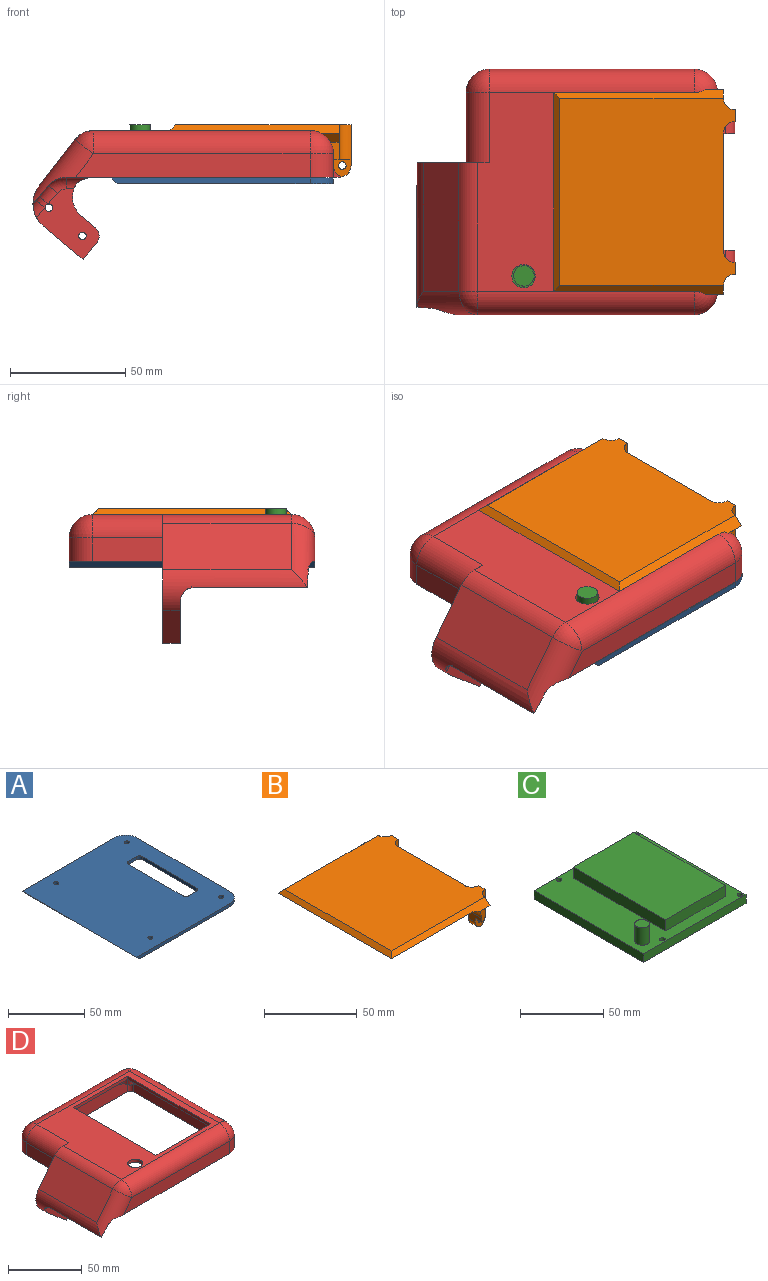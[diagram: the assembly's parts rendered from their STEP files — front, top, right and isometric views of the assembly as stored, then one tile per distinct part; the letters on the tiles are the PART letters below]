
ASSEMBLY  parts=4 mates=3
PART A: 20 faces, bbox 96.5x106.7x2.5 mm
  f0: plane 106.68x96.52mm, normal (0,0,1), area 9514.1mm2, adj f2,f3,f4,f5,f6,f7,f8,f9
  f1: plane 106.68x93.98mm, normal (0,0,-1), area 9243.1mm2, adj f2,f3,f4,f5,f6,f7,f8,f9
  f2: plane 86.36x2.54mm, normal (0,-1,0), area 216.1mm2, adj f0,f1,f17,f19
  f3: plane 86.36x2.54mm, normal (1,0,0), area 219.4mm2, adj f0,f1,f17,f18
  f4: plane 86.36x2.54mm, normal (0,1,0), area 216.1mm2, adj f0,f1,f18,f19
  f5: cylinder r=1.65mm len=3.3mm, axis (0,0,-1), area 26.3mm2, adj f0,f1
  f6: cylinder r=1.65mm len=3.3mm, axis (0,0,-1), area 26.3mm2, adj f0,f1
  f7: cylinder r=1.65mm len=3.3mm, axis (0,0,-1), area 26.3mm2, adj f0,f1
  f8: cylinder r=1.65mm len=3.3mm, axis (0,0,-1), area 26.3mm2, adj f0,f1
  f9: plane 50.8x2.54mm, normal (1,0,0), area 129mm2, adj f0,f1,f13,f16
  f10: plane 7.62x2.54mm, normal (0,-1,0), area 19.4mm2, adj f0,f1,f15,f16
  f11: plane 50.8x2.54mm, normal (-1,0,0), area 129mm2, adj f0,f1,f14,f15
  f12: plane 7.62x2.54mm, normal (0,1,0), area 19.4mm2, adj f0,f1,f13,f14
  f13: cylinder r=2.54mm len=2.54mm, axis (0,0,1), area 10.1mm2, adj f0,f1,f9,f12
  f14: cylinder r=2.54mm len=2.54mm, axis (0,0,-1), area 10.1mm2, adj f0,f1,f11,f12
  f15: cylinder r=2.54mm len=2.54mm, axis (0,0,1), area 10.1mm2, adj f0,f1,f10,f11
  f16: cylinder r=2.54mm len=2.54mm, axis (0,0,-1), area 10.1mm2, adj f0,f1,f9,f10
  f17: cylinder r=10.16mm len=10.16mm, axis (0,0,-1), area 40.5mm2, adj f0,f1,f2,f3
  f18: cylinder r=10.16mm len=10.16mm, axis (0,0,1), area 40.5mm2, adj f0,f1,f3,f4
  f19: plane 106.68x2.54mm, normal (-0.71,0,-0.71), area 383.2mm2, adj f0,f1,f2,f4
PART B: 43 faces, bbox 78.7x88.9x22.7 mm
  f0: plane 7.62x3.9mm, normal (0,-1,0), area 21.6mm2, adj f7,f24,f25,f27,f42
  f1: plane 7.62x3.9mm, normal (0,1,0), area 21.6mm2, adj f3,f8,f25,f26,f41
  f2: plane 49.69x2.54mm, normal (-1,0,0), area 119.7mm2, adj f4,f25,f34,f35
  f3: plane 10.03x5.08mm, normal (-1,0,0), area 38.4mm2, adj f1,f8,f10,f11,f21,f25
  f4: plane 40.89x2.54mm, normal (0,0,-1), area 103.9mm2, adj f2,f9,f34,f35
  f5: cylinder r=5.08mm len=12.7mm, axis (0,0,-1), area 100.7mm2, adj f9,f15,f16,f31,f32
  f6: cylinder r=5.08mm len=12.7mm, axis (0,0,1), area 100.7mm2, adj f9,f15,f17,f29,f33
  f7: plane 10.03x5.08mm, normal (-1,0,0), area 38.4mm2, adj f0,f12,f13,f23,f24,f25
  f8: plane 7.62x4.95mm, normal (0,0,-1), area 18.1mm2, adj f1,f3,f10,f26
  f9: plane 51.05x15.24mm, normal (1,0,0), area 767.8mm2, adj f4,f5,f6,f15,f32,f33,f34,f35
  f10: plane 22.7x7.62mm, normal (0,1,0), area 38.6mm2, adj f3,f8,f15,f16,f19,f20,f21,f26
  f11: plane 13.39x8.2mm, normal (0,-1,0), area 61mm2, adj f3,f16,f19,f20,f21,f25,f31,f32
  f12: plane 13.39x8.2mm, normal (0,1,0), area 61mm2, adj f7,f17,f18,f22,f23,f25,f29,f33
  f13: plane 22.7x7.62mm, normal (0,-1,0), area 38.6mm2, adj f7,f15,f17,f18,f22,f23,f24,f27
  f14: plane 86.36x60.96mm, normal (0,0,-1), area 5264.5mm2, adj f25,f38,f39,f40
  f15: plane 81.28x76.2mm, normal (0,0,1), area 5854.4mm2, adj f5,f6,f9,f10,f13,f16,f17,f26
  f16: plane 17.78x5.08mm, normal (1,0,0), area 90.3mm2, adj f5,f10,f11,f15,f20
  f17: plane 17.78x5.08mm, normal (1,0,0), area 90.3mm2, adj f6,f12,f13,f15,f22
  f18: cylinder r=1.65mm len=5.08mm, axis (0,-1,0), area 52.7mm2, adj f12,f13
  f19: cylinder r=1.65mm len=5.08mm, axis (0,-1,0), area 52.7mm2, adj f10,f11
  f20: cylinder r=5.08mm len=5.08mm, axis (0,-1,0), area 34mm2, adj f10,f11,f16,f21
  f21: cylinder r=5.08mm len=5.08mm, axis (0,-1,0), area 34mm2, adj f3,f10,f11,f20
  f22: cylinder r=5.08mm len=5.08mm, axis (0,-1,0), area 34mm2, adj f12,f13,f17,f23
  f23: cylinder r=5.08mm len=5.08mm, axis (0,-1,0), area 34mm2, adj f7,f12,f13,f22
  f24: plane 7.62x4.95mm, normal (0,0,-1), area 18.1mm2, adj f0,f7,f13,f27
  f25: cylinder r=10.16mm len=88.9mm, axis (0,1,0), area 1314.3mm2, adj f0,f1,f2,f3,f7,f11,f12,f14
  f26: cylinder r=5.08mm len=15.24mm, axis (0,0,1), area 119.7mm2, adj f1,f8,f10,f15,f36
  f27: cylinder r=5.08mm len=15.24mm, axis (0,0,1), area 119.7mm2, adj f0,f13,f15,f24,f37
  f28: plane 0.85x0.39mm, normal (0,-1,0), area 0mm2, adj f25,f33,f35
  f29: plane 3.41x1.32mm, normal (0,0,-1), area 1.4mm2, adj f6,f12,f33
  f30: plane 0.85x0.39mm, normal (0,1,0), area 0mm2, adj f25,f32,f34
  f31: plane 3.41x1.32mm, normal (0,0,-1), area 1.4mm2, adj f5,f11,f32
  f32: cylinder r=5.08mm len=5.61mm, axis (0,1,0), area 28.1mm2, adj f5,f9,f11,f25,f30,f31,f34
  f33: cylinder r=5.08mm len=5.61mm, axis (0,1,0), area 28.1mm2, adj f6,f9,f12,f25,f28,f29,f35
  f34: cylinder r=5.08mm len=5.08mm, axis (-1,0,0), area 16.6mm2, adj f2,f4,f9,f25,f30,f32
  f35: cylinder r=5.08mm len=5.08mm, axis (1,0,0), area 16.6mm2, adj f2,f4,f9,f25,f28,f33
  f36: plane 7.62x3.81mm, normal (1,0,0), area 14.5mm2, adj f26,f40,f41
  f37: plane 7.62x3.81mm, normal (1,0,0), area 14.5mm2, adj f27,f38,f42
  f38: plane 73.66x3.81mm, normal (0,-0.71,0.71), area 276.9mm2, adj f14,f15,f25,f37,f39,f42
  f39: plane 86.36x2.54mm, normal (-0.71,0,0.71), area 301.1mm2, adj f14,f15,f38,f40
  f40: plane 73.66x3.81mm, normal (0,0.71,0.71), area 276.9mm2, adj f14,f15,f25,f36,f39,f41
  f41: plane 7.78x3.81mm, normal (0,0.71,-0.71), area 29.6mm2, adj f1,f25,f36,f40
  f42: plane 7.78x3.81mm, normal (0,-0.71,-0.71), area 29.6mm2, adj f0,f25,f37,f38
PART C: 17 faces, bbox 87.1x93.2x19.1 mm
  f0: plane 87.12x6.35mm, normal (0,1,0), area 553.2mm2, adj f1,f7,f8,f9
  f1: plane 93.22x6.35mm, normal (-1,0,0), area 591.9mm2, adj f0,f2,f8,f9
  f2: plane 87.12x6.35mm, normal (0,-1,0), area 553.2mm2, adj f1,f7,f8,f9
  f3: cylinder r=1.65mm len=6.35mm, axis (0,0,-1), area 65.9mm2, adj f8,f9
  f4: cylinder r=1.65mm len=6.35mm, axis (0,0,-1), area 65.9mm2, adj f8,f9
  f5: cylinder r=1.65mm len=6.35mm, axis (0,0,-1), area 65.9mm2, adj f8,f9
  f6: cylinder r=1.65mm len=6.35mm, axis (0,0,-1), area 65.9mm2, adj f8,f9
  f7: plane 93.22x6.35mm, normal (1,0,0), area 591.9mm2, adj f0,f2,f8,f9
  f8: plane 93.22x87.12mm, normal (0,0,1), area 4047mm2, adj f0,f1,f2,f3,f4,f5,f6,f7
  f9: plane 93.22x87.12mm, normal (0,0,-1), area 8087.1mm2, adj f0,f1,f2,f3,f4,f5,f6,f7
  f10: plane 78x8.13mm, normal (1,0,0), area 634mm2, adj f8,f11,f13,f14
  f11: plane 51x8.13mm, normal (0,1,0), area 414.5mm2, adj f8,f10,f12,f14
  f12: plane 78x8.13mm, normal (-1,0,0), area 634mm2, adj f8,f11,f13,f14
  f13: plane 51x8.13mm, normal (0,-1,0), area 414.5mm2, adj f8,f10,f12,f14
  f14: plane 78x51mm, normal (0,0,1), area 3978mm2, adj f10,f11,f12,f13
  f15: cylinder r=4.45mm len=12.7mm, axis (0,0,-1), area 354.7mm2, adj f8,f16
  f16: plane 8.89x8.89mm, normal (0,0,1), area 62.1mm2, adj f15
PART D: 86 faces, bbox 140.6x106.8x56.1 mm
  f0: plane 12.7x10.16mm, normal (1,0,0), area 129mm2, adj f34,f55,f70,f78
  f1: plane 12.7x10.16mm, normal (1,0,0), area 129mm2, adj f34,f54,f70,f75
  f2: plane 94.08x86.36mm, normal (0,0,1), area 3736.2mm2, adj f8,f21,f22,f23,f24,f25,f53,f66
  f3: plane 17.38x7.02mm, normal (0,0,-1), area 48.2mm2, adj f12,f26,f37,f58,f59
  f4: plane 11.98x11.92mm, normal (0,0,-1), area 46.3mm2, adj f13,f28,f37,f38,f56,f60,f61
  f5: plane 11.98x11.92mm, normal (0,0,-1), area 46.3mm2, adj f14,f30,f35,f38,f57,f62,f63
  f6: plane 17.38x7.02mm, normal (0,0,-1), area 48.2mm2, adj f15,f32,f35,f64,f65
  f7: plane 17.2x14.43mm, normal (-0.64,0,-0.77), area 171.1mm2, adj f8,f41,f42,f85
  f8: plane 55.96x31.46mm, normal (0,1,0), area 736.3mm2, adj f2,f7,f10,f19,f20,f34,f39,f40
  f9: plane 50.65x8.07mm, normal (0.77,0,-0.64), area 520.1mm2, adj f43,f48,f50,f51,f74,f85
  f10: plane 30.48x10.16mm, normal (-1,0,0), area 309.7mm2, adj f8,f34,f52,f66
  f11: plane 94.23x89.41mm, normal (0,0,-1), area 3968.5mm2, adj f12,f13,f14,f15,f21,f22,f23,f24
  f12: cylinder r=3.81mm len=7.62mm, axis (0,0,1), area 78.9mm2, adj f3,f11,f58,f59
  f13: cylinder r=3.81mm len=7.62mm, axis (0,0,1), area 33.6mm2, adj f4,f11,f60,f61
  f14: cylinder r=3.81mm len=7.62mm, axis (0,0,1), area 33.6mm2, adj f5,f11,f62,f63
  f15: cylinder r=3.81mm len=7.62mm, axis (0,0,1), area 78.9mm2, adj f6,f11,f64,f65
  f16: plane 50.8x10.16mm, normal (1,0,0), area 516.1mm2, adj f34,f70,f76,f77
  f17: plane 88.9x10.16mm, normal (0,1,0), area 903.2mm2, adj f34,f52,f54,f68
  f18: plane 101.97x10.16mm, normal (0,-1,0), area 995.9mm2, adj f34,f55,f72,f74
  f19: cylinder r=1.65mm len=7.62mm, axis (0,1,0), area 79mm2, adj f8,f42,f50
  f20: cylinder r=1.65mm len=7.62mm, axis (0,1,0), area 79mm2, adj f8,f42
  f21: cylinder r=5.08mm len=10.16mm, axis (0,0,1), area 81.1mm2, adj f2,f11
  f22: plane 79.5x2.54mm, normal (1,0,0), area 201.9mm2, adj f2,f11,f23,f25
  f23: plane 52.2x2.54mm, normal (0,1,0), area 132.6mm2, adj f2,f11,f22,f24
  f24: plane 79.5x2.54mm, normal (-1,0,0), area 201.9mm2, adj f2,f11,f23,f25
  f25: plane 52.2x2.54mm, normal (0,-1,0), area 132.6mm2, adj f2,f11,f22,f24
  f26: cylinder r=1.65mm len=7.62mm, axis (0,0,1), area 79mm2, adj f3,f27
  f27: plane 3.3x3.3mm, normal (0,0,-1), area 8.6mm2, adj f26
  f28: cylinder r=1.65mm len=7.62mm, axis (0,0,1), area 79mm2, adj f4,f29
  f29: plane 3.3x3.3mm, normal (0,0,-1), area 8.6mm2, adj f28
  f30: cylinder r=1.65mm len=7.62mm, axis (0,0,1), area 79mm2, adj f5,f31
  f31: plane 3.3x3.3mm, normal (0,0,-1), area 8.6mm2, adj f30
  f32: cylinder r=1.65mm len=7.62mm, axis (0,0,1), area 79mm2, adj f6,f33
  f33: plane 3.3x3.3mm, normal (0,0,-1), area 8.6mm2, adj f32
  f34: plane 118.66x106.71mm, normal (0,0,-1), area 3493.8mm2, adj f0,f1,f8,f10,f16,f17,f18,f35
  f35: plane 86.87x17.78mm, normal (0,-1,0), area 1340.1mm2, adj f5,f6,f11,f34,f36,f57,f63,f64
  f36: plane 94.23x17.78mm, normal (1,0,0), area 1675.5mm2, adj f11,f34,f35,f37
  f37: plane 86.87x17.78mm, normal (0,1,0), area 1340.1mm2, adj f3,f4,f11,f34,f36,f56,f58,f59
  f38: plane 89.15x17.78mm, normal (-1,0,0), area 1442.2mm2, adj f4,f5,f11,f34,f56,f57,f61,f62
  f39: plane 55.88x20.08mm, normal (-0.79,0,0.61), area 1420.3mm2, adj f8,f53,f74,f85
  f40: plane 7.62x6.13mm, normal (0.64,0,0.77), area 61mm2, adj f8,f42,f44,f46
  f41: plane 7.62x6.89mm, normal (0.77,0,-0.64), area 68.5mm2, adj f7,f8,f42,f46
  f42: plane 30.56x27.13mm, normal (0,-1,0), area 395.8mm2, adj f7,f19,f20,f40,f41,f44,f46,f47
  f43: cylinder r=10.16mm len=52.85mm, axis (0,1,0), area 456.7mm2, adj f9,f34,f49,f74
  f44: cylinder r=10.16mm len=13.54mm, axis (0,-1,0), area 114.8mm2, adj f8,f40,f42,f45,f47
  f45: cylinder r=10.16mm len=12.7mm, axis (0,-1,0), area 80.1mm2, adj f8,f34,f44,f47
  f46: cylinder r=5.08mm len=7.62mm, axis (0,1,0), area 60.8mm2, adj f8,f40,f41,f42
  f47: cylinder r=5.08mm len=11.6mm, axis (-1,0,0), area 53.5mm2, adj f34,f42,f44,f45,f49
  f48: cylinder r=5.08mm len=7.63mm, axis (-0.64,0,-0.77), area 29.2mm2, adj f9,f42,f50,f85
  f49: torus R=5.08mm, axis (0,1,0), area 57.9mm2, adj f42,f43,f47,f51
  f50: bspline ~5.25x5.08mm, area 16.3mm2, adj f9,f19,f48,f51
  f51: cylinder r=5.08mm len=7.98mm, axis (-0.64,0,-0.77), area 49.1mm2, adj f9,f42,f49,f50
  f52: cylinder r=10.16mm len=10.16mm, axis (0,0,-1), area 162.1mm2, adj f10,f17,f34,f67
  f53: cylinder r=10.16mm len=55.88mm, axis (0,-1,0), area 517.2mm2, adj f2,f8,f39,f73
  f54: cylinder r=10.16mm len=10.16mm, axis (0,0,1), area 162.1mm2, adj f1,f17,f34,f69
  f55: cylinder r=10.16mm len=10.16mm, axis (0,0,-1), area 162.1mm2, adj f0,f18,f34,f71
  f56: cylinder r=2.54mm len=10.16mm, axis (0,0,-1), area 40.5mm2, adj f4,f34,f37,f38
  f57: cylinder r=2.54mm len=10.16mm, axis (0,0,-1), area 40.5mm2, adj f5,f34,f35,f38
  f58: cylinder r=5.08mm len=7.62mm, axis (0,0,1), area 52.6mm2, adj f3,f11,f12,f37
  f59: cylinder r=5.08mm len=7.62mm, axis (0,0,1), area 52.6mm2, adj f3,f11,f12,f37
  f60: cylinder r=5.08mm len=7.62mm, axis (0,0,1), area 52.6mm2, adj f4,f11,f13,f37
  f61: cylinder r=5.08mm len=7.62mm, axis (0,0,1), area 53mm2, adj f4,f11,f13,f38
  f62: cylinder r=5.08mm len=7.62mm, axis (0,0,1), area 53mm2, adj f5,f11,f14,f38
  f63: cylinder r=5.08mm len=7.62mm, axis (0,0,1), area 52.6mm2, adj f5,f11,f14,f35
  f64: cylinder r=5.08mm len=7.62mm, axis (0,0,1), area 52.6mm2, adj f6,f11,f15,f35
  f65: cylinder r=5.08mm len=7.62mm, axis (0,0,1), area 52.6mm2, adj f6,f11,f15,f35
  f66: cylinder r=10.16mm len=30.48mm, axis (0,-1,0), area 486.4mm2, adj f2,f8,f10,f67
  f67: sphere r=10.16mm, area 162.1mm2, adj f52,f66,f68
  f68: cylinder r=10.16mm len=88.9mm, axis (1,0,0), area 1418.8mm2, adj f2,f17,f67,f69
  f69: sphere r=10.16mm, area 162.1mm2, adj f54,f68,f70
  f70: cylinder r=10.16mm len=86.36mm, axis (0,-1,0), area 1344.2mm2, adj f0,f1,f2,f16,f69,f71,f75,f76
  f71: sphere r=10.16mm, area 162.1mm2, adj f55,f70,f72
  f72: cylinder r=10.16mm len=94.08mm, axis (-1,0,0), area 1501.5mm2, adj f2,f18,f71,f73
  f73: sphere r=10.16mm, area 94mm2, adj f53,f72,f74
  f74: cylinder r=10.16mm len=32.51mm, axis (-0.61,0,-0.79), area 365.9mm2, adj f9,f18,f34,f39,f43,f73,f85
  f75: plane 13.45x8.17mm, normal (0,1,0), area 60.4mm2, adj f1,f34,f70,f80,f82,f84
  f76: plane 13.45x8.17mm, normal (0,-1,0), area 60.4mm2, adj f16,f34,f70,f80,f82,f84
  f77: plane 13.45x8.17mm, normal (0,1,0), area 60.4mm2, adj f16,f34,f70,f79,f81,f83
  f78: plane 13.45x8.17mm, normal (0,-1,0), area 60.4mm2, adj f0,f34,f70,f79,f81,f83
  f79: cylinder r=1.65mm len=5.08mm, axis (0,1,0), area 52.7mm2, adj f77,f78
  f80: cylinder r=1.65mm len=5.08mm, axis (0,1,0), area 52.7mm2, adj f75,f76
  f81: cylinder r=5.08mm len=10.09mm, axis (0,-1,0), area 76.7mm2, adj f34,f77,f78,f83
  f82: cylinder r=5.08mm len=10.09mm, axis (0,-1,0), area 76.7mm2, adj f34,f75,f76,f84
  f83: cylinder r=5.08mm len=5.08mm, axis (0,1,0), area 27.6mm2, adj f70,f77,f78,f81
  f84: cylinder r=5.08mm len=5.08mm, axis (0,1,0), area 27.6mm2, adj f70,f75,f76,f82
  f85: cylinder r=12.7mm len=62.79mm, axis (0,-1,0), area 594.3mm2, adj f7,f8,f9,f39,f42,f48,f74
PLACE A t=(-58.15,38.28,39.13)mm
PLACE B t=(66.47,52.06,62.24)mm
PLACE C t=(-15.56,66.11,45.73)mm
PLACE D t=(-62.12,-135.2,59.7)mm
MATE parallel A.f5 <-> C.f4  axis (0,0,1) through (44.03,12.82,41.67)mm
MATE parallel C.f4 <-> D.f13  axis (0,0,1) through (44.03,12.82,52.08)mm
MATE parallel B.f18 <-> D.f79  axis (0,-1,0) through (56.28,87.34,47)mm
